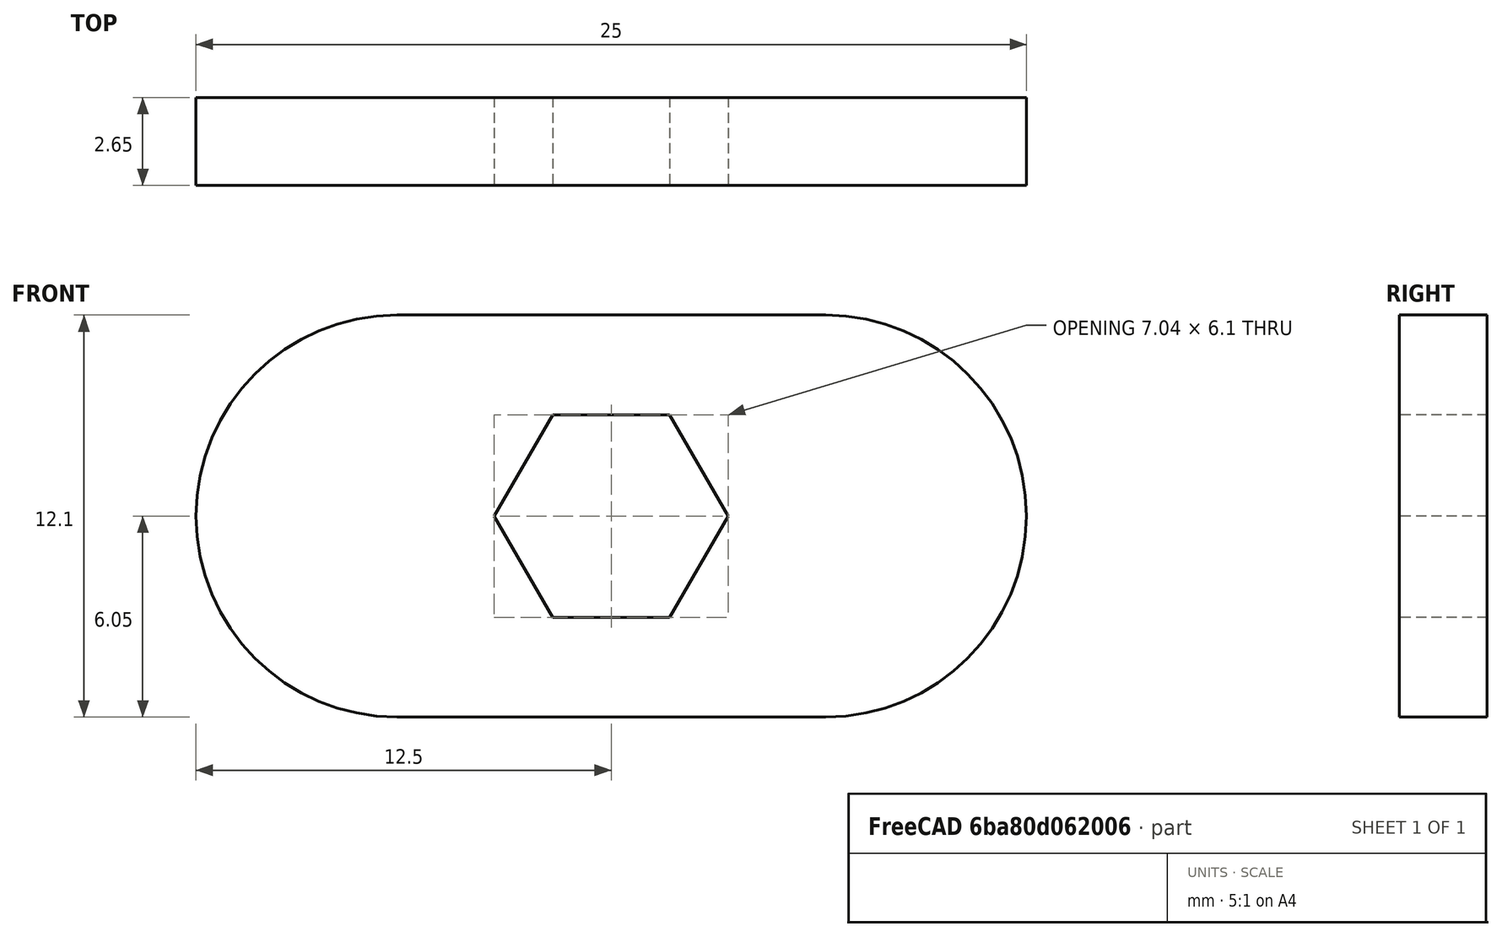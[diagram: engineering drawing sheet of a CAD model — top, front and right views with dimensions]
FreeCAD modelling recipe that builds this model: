
FCSTD DOCUMENT  (FreeCAD 0.20R29603 (Git))
Label: porca
License: All rights reserved
LicenseURL: http://en.wikipedia.org/wiki/All_rights_reserved
objects: Sketcher::SketchObject×1, PartDesign::Pad×1, PartDesign::Body×1
note: 4 computed .brp shape members not serialized (recipe doc carries the construction recipe); baked Part::Feature solids carry a one-line shape summary decoded from their .brp

FEATURE [Sketcher::SketchObject] Sketch
  FullyConstrained = true
  MapMode = 5
  Placement = pos=(0,0,0) rot=(1,0,0;1.5708rad)
  Support = -> [XZ_Plane]
  sketch-geometry (15):
    g0: LineSegment StartX=1.76092 StartY=3.05 StartZ=0 EndX=-1.76092 EndY=3.05 EndZ=0
    g1: LineSegment StartX=-1.76092 StartY=3.05 StartZ=0 EndX=-3.52184 EndY=4e-16 EndZ=0
    g2: LineSegment StartX=-3.52184 StartY=4e-16 StartZ=0 EndX=-1.76092 EndY=-3.05 EndZ=0
    g3: LineSegment StartX=-1.76092 StartY=-3.05 StartZ=0 EndX=1.76092 EndY=-3.05 EndZ=0
    g4: LineSegment StartX=1.76092 StartY=-3.05 StartZ=0 EndX=3.52184 EndY=0 EndZ=0
    g5: LineSegment StartX=3.52184 StartY=0 StartZ=0 EndX=1.76092 EndY=3.05 EndZ=0
    g6: Circle CenterX=0 CenterY=0 CenterZ=0 NormalX=0 NormalY=0 NormalZ=1 AngleXU=0 Radius=3.52184
    g7: ArcOfCircle CenterX=-6.45 CenterY=0 CenterZ=0 NormalX=0 NormalY=0 NormalZ=1 AngleXU=0 Radius=6.05 StartAngle=1.5708 EndAngle=4.71239
    g8: ArcOfCircle CenterX=6.45 CenterY=0 CenterZ=0 NormalX=0 NormalY=0 NormalZ=1 AngleXU=0 Radius=6.05 StartAngle=4.71239 EndAngle=7.85398
    g9: LineSegment StartX=-6.45 StartY=-6.05 StartZ=0 EndX=6.45 EndY=-6.05 EndZ=0
    g10: LineSegment StartX=6.45 StartY=6.05 StartZ=0 EndX=-6.45 EndY=6.05 EndZ=0
    g11: LineSegment StartX=-6.45 StartY=0 StartZ=0 EndX=0 EndY=0 EndZ=0
    g12: LineSegment StartX=0 StartY=0 StartZ=0 EndX=6.45 EndY=0 EndZ=0
    g13: GeomPoint X=-12.5 Y=0 Z=0
    g14: GeomPoint X=12.5 Y=0 Z=0
  constraints (35):
    c: Coincident(g0,g1)
    c: Coincident(g1,g2)
    c: Coincident(g2,g3)
    c: Coincident(g3,g4)
    c: Coincident(g4,g5)
    c: Coincident(g5,g0)
    c: Equal(g0, g1-g5) x5
    c: PointOnObject(g0,g6)
    c: PointOnObject(g1,g6)
    c: PointOnObject(g2,g6)
    c: PointOnObject(g3,g6)
    c: PointOnObject(g4,g6)
    c: PointOnObject(g5,g6)
    c: Coincident(g6,g-1)
    c: DistanceY(g2,g0) = 6.1
    c: Horizontal(g0)
    c: Tangent(g7,g9) = -1.5708
    c: Tangent(g9,g8) = -1.5708
    c: Tangent(g8,g10) = -1.5708
    c: Tangent(g10,g7) = -1.5708
    c: Equal(g7,g8)
    c: PointOnObject(g7,g-1)
    c: PointOnObject(g8,g-1)
    c: Coincident(g11,g7)
    c: PointOnObject(g11,g-2)
    c: Coincident(g12,g11)
    c: Coincident(g12,g8)
    c: Equal(g12,g11)
    c: PointOnObject(g11,g-1)
    c: PointOnObject(g14,g8)
    c: PointOnObject(g14,g-1)
    c: PointOnObject(g13,g7)
    c: PointOnObject(g13,g-1)
    c: DistanceX(g13,g14) = 25
    c: DistanceY(g8,g3) = 3
FEATURE [PartDesign::Pad] Pad
  Direction = (0,-1,2e-16)
  Length = 2.65
  Length2 = 10
  Placement = pos=(0,0,0) rot=(1,0,0;1.5708rad)
  Profile = -> Sketch
  ReferenceAxis = -> Sketch [N_Axis]
  Type = 0
FEATURE [PartDesign::Body] Body
  Group = -> [Sketch,Pad]
  Origin = -> Origin
  Tip = -> Pad
